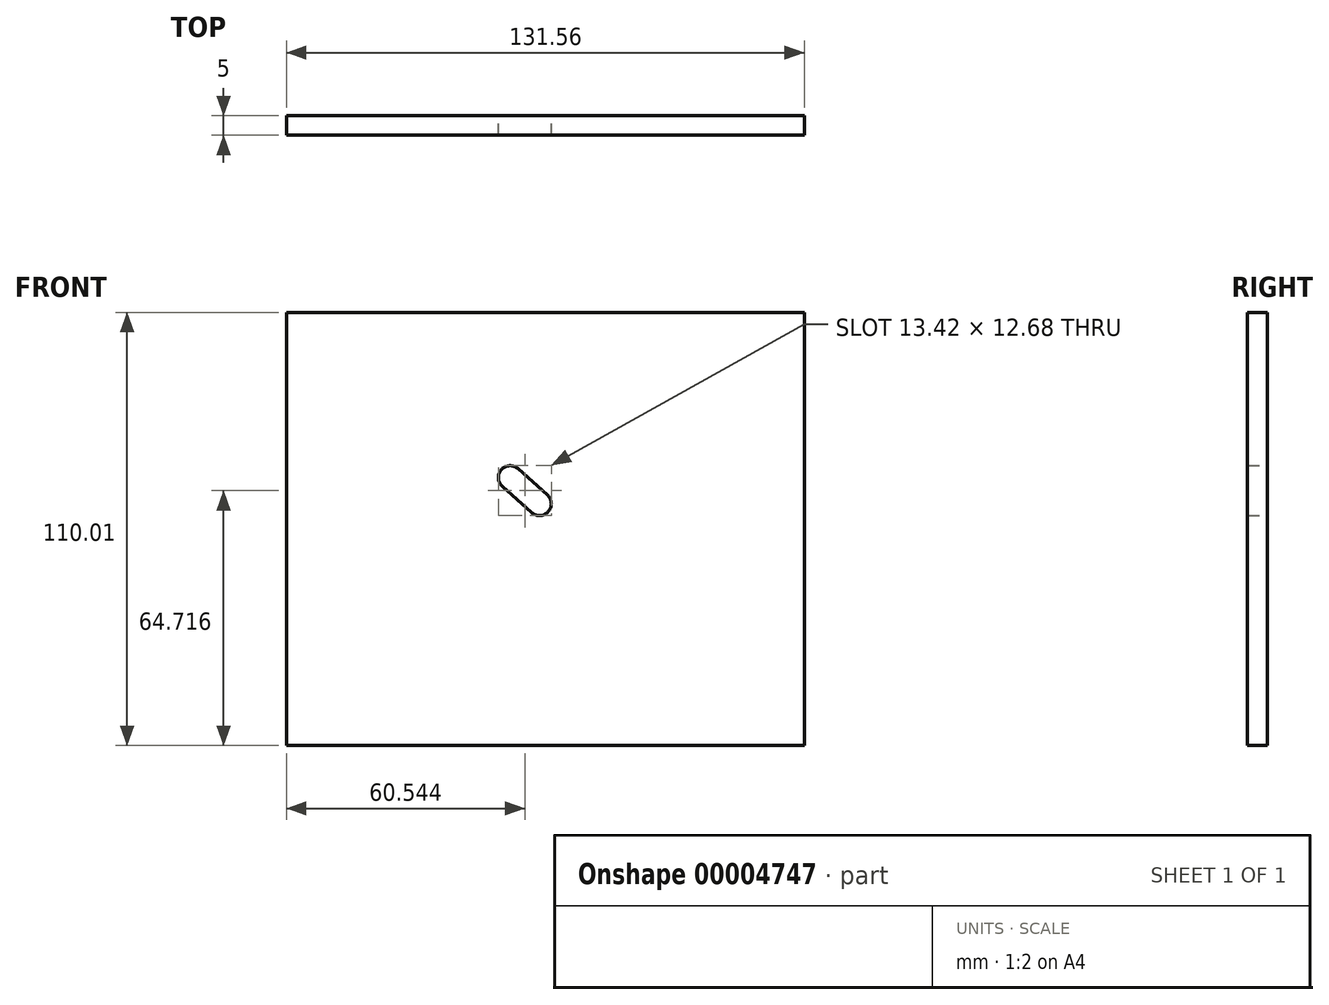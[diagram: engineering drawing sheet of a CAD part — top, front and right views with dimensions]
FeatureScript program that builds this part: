
annotation { "Feature Type Name" : "Feature", "Feature Type Description" : "" }
export const myFeature = defineFeature(function(context is Context, id is Id, definition is map)
    precondition{}
    {
        {
            var Q0;
            Q0=qCreatedBy(makeId("Front.planeOp"),FACE);
            var sketch = newSketch(context, id + "F0", { "sketchPlane" : qUnion([Q0])});
            skLineSegment(sketch, "E0.bottom", {"start": v(-64.26, 48.64) * mm, "end": v(67.3, 48.64) * mm});
            skLineSegment(sketch, "E0.top", {"start": v(-64.26, -61.37) * mm, "end": v(67.3, -61.37) * mm});
            skLineSegment(sketch, "E0.left", {"start": v(-64.26, 48.64) * mm, "end": v(-64.26, -61.37) * mm});
            skLineSegment(sketch, "E0.right", {"start": v(67.3, 48.64) * mm, "end": v(67.3, -61.37) * mm});
            skSolve(sketch);
        }
        {
            var Q0;
            Q0=makeQuery(id+"F0.imprint","IMPRINT",FACE,{"disambiguationData":[TD([[makeQuery(id+"F0.imprint","IMPRINT",EDGE,{"derivedFrom":sQuery(id+"F0.wireOp",EDGE,"E0.bottom")}),-1.0]])]});
            extrude(context, id + "F1", {"entities" : qUnion([Q0]), "depth" : 5 * mm});
        }
        {
            var Q0;
            Q0=qCreatedBy(makeId("Front.planeOp"),FACE);
            var sketch = newSketch(context, id + "F2", { "sketchPlane" : qUnion([Q0])});
            skLineSegment(sketch, "E1.bottom", {"start": v(-9.44, 4.46) * mm, "end": v(-2, -2.23) * mm});
            skLineSegment(sketch, "E1.top", {"start": v(-5.42, 8.92) * mm, "end": v(2, 2.23) * mm});
            skLineSegment(sketch, "E1.left", {"start": v(2, 2.23) * mm, "end": v(-2, -2.23) * mm});
            skLineSegment(sketch, "E1.right", {"start": v(-5.42, 8.92) * mm, "end": v(-9.44, 4.46) * mm});
            skCircle(sketch, "E2", {"center": v(0, 0) * mm, "radius": 3 * mm});
            skCircle(sketch, "E3", {"center": v(-7.43, 6.7) * mm, "radius": 3 * mm});
            skSolve(sketch);
        }
        {
            var Q0;
            Q0 = qSketchRegion(id + "F2", true);
            extrude(context, id + "F3", {"entities" : qUnion([Q0]), "operationType" : NewBodyOperationType.REMOVE, "depth" : 25 * mm});
        }
    });
